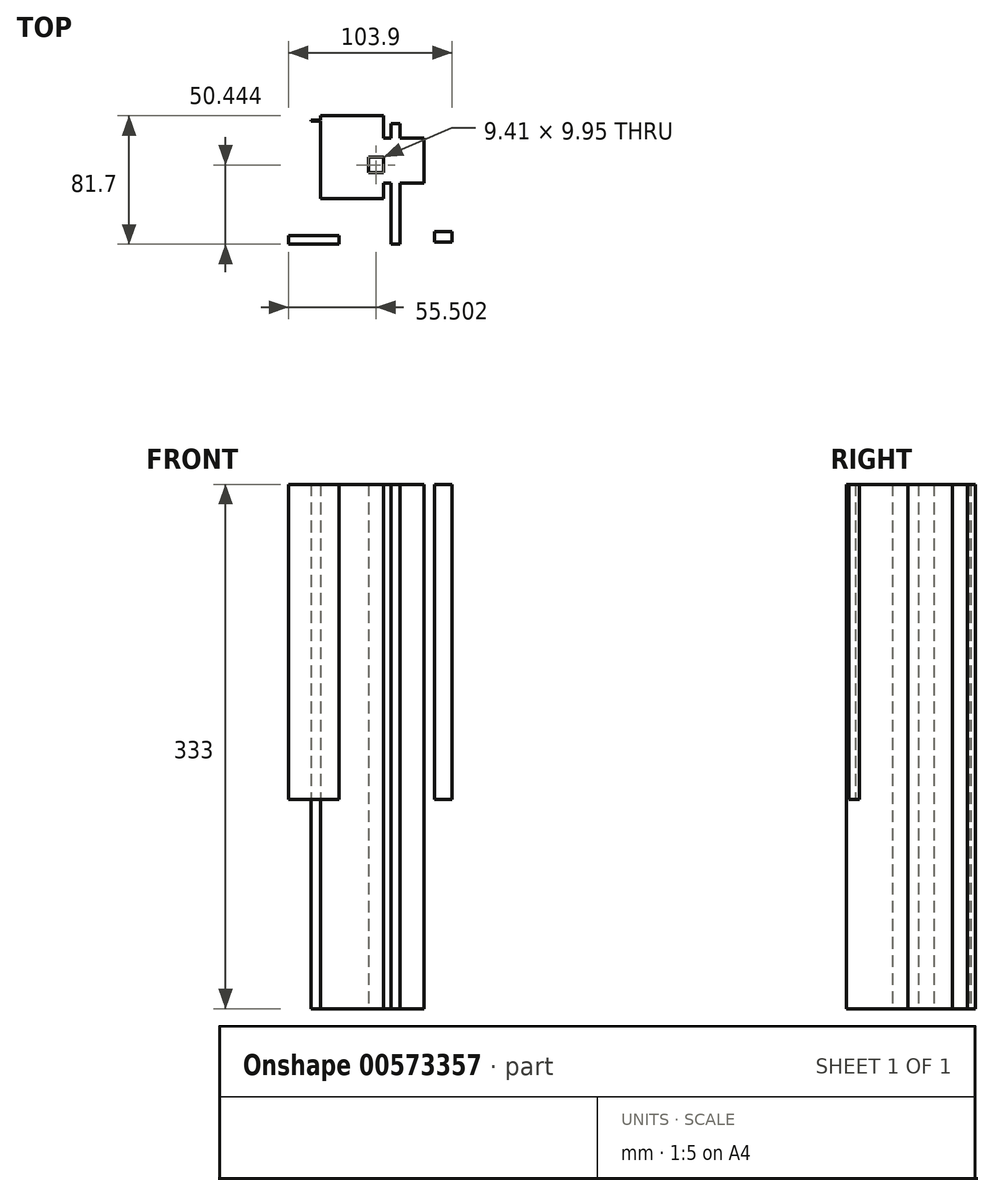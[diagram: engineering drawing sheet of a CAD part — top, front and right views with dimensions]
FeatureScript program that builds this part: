
annotation { "Feature Type Name" : "Feature", "Feature Type Description" : "" }
export const myFeature = defineFeature(function(context is Context, id is Id, definition is map)
    precondition{}
    {
        {
            var Q0;
            Q0=qCreatedBy(makeId("Top.planeOp"),FACE);
            var sketch = newSketch(context, id + "F0", { "sketchPlane" : qUnion([Q0])});
            skLineSegment(sketch, "E0.bottom", {"start": v(33.03, 37.83) * mm, "end": v(38.9, 37.83) * mm});
            skLineSegment(sketch, "E0.top", {"start": v(33.03, -38.9) * mm, "end": v(38.9, -38.9) * mm});
            skLineSegment(sketch, "E0.left", {"start": v(33.03, 37.83) * mm, "end": v(33.03, -38.9) * mm});
            skLineSegment(sketch, "E0.right", {"start": v(38.9, 37.83) * mm, "end": v(38.9, -38.9) * mm});
            skLineSegment(sketch, "E1.bottom", {"start": v(0, -33.21) * mm, "end": v(-31.97, -33.21) * mm});
            skLineSegment(sketch, "E1.top", {"start": v(0, -38.9) * mm, "end": v(-31.97, -38.9) * mm});
            skLineSegment(sketch, "E1.left", {"start": v(0, -33.21) * mm, "end": v(0, -38.9) * mm});
            skLineSegment(sketch, "E1.right", {"start": v(-31.97, -33.21) * mm, "end": v(-31.97, -38.9) * mm});
            skLineSegment(sketch, "E2.bottom", {"start": v(-9.95, 39.25) * mm, "end": v(-17.58, 39.25) * mm});
            skLineSegment(sketch, "E2.top", {"start": v(-9.95, 39.96) * mm, "end": v(-17.58, 39.96) * mm});
            skLineSegment(sketch, "E2.left", {"start": v(-9.95, 39.25) * mm, "end": v(-9.95, 39.96) * mm});
            skLineSegment(sketch, "E2.right", {"start": v(-17.58, 39.25) * mm, "end": v(-17.58, 39.96) * mm});
            skLineSegment(sketch, "E3.bottom", {"start": v(-11.72, -9.77) * mm, "end": v(28.24, -9.77) * mm});
            skLineSegment(sketch, "E3.top", {"start": v(-11.72, 42.8) * mm, "end": v(28.24, 42.8) * mm});
            skLineSegment(sketch, "E3.left", {"start": v(-11.72, -9.77) * mm, "end": v(-11.72, 42.8) * mm});
            skLineSegment(sketch, "E3.right", {"start": v(28.24, -9.77) * mm, "end": v(28.24, 42.8) * mm});
            skPoint(sketch, "E4.oppositeSnap0", {"position": v(28.24, 16.52) * mm});
            skLineSegment(sketch, "E4.bottom", {"start": v(28.24, 6.57) * mm, "end": v(18.83, 6.57) * mm});
            skLineSegment(sketch, "E4.top", {"start": v(28.24, 16.52) * mm, "end": v(18.83, 16.52) * mm});
            skLineSegment(sketch, "E4.left", {"start": v(28.24, 6.57) * mm, "end": v(28.24, 16.52) * mm});
            skLineSegment(sketch, "E4.right", {"start": v(18.83, 6.57) * mm, "end": v(18.83, 16.52) * mm});
            skLineSegment(sketch, "E5.bottom", {"start": v(71.93, -30.73) * mm, "end": v(60.92, -30.73) * mm});
            skLineSegment(sketch, "E5.top", {"start": v(71.93, -37.47) * mm, "end": v(60.92, -37.47) * mm});
            skLineSegment(sketch, "E5.left", {"start": v(71.93, -30.73) * mm, "end": v(71.93, -37.47) * mm});
            skLineSegment(sketch, "E5.right", {"start": v(60.92, -30.73) * mm, "end": v(60.92, -37.47) * mm});
            skLineSegment(sketch, "E6.bottom", {"start": v(54.17, 0) * mm, "end": v(13.68, 0) * mm});
            skLineSegment(sketch, "E6.top", {"start": v(54.17, 28.42) * mm, "end": v(13.68, 28.42) * mm});
            skLineSegment(sketch, "E6.left", {"start": v(54.17, 0) * mm, "end": v(54.17, 28.42) * mm});
            skLineSegment(sketch, "E6.right", {"start": v(13.68, 0) * mm, "end": v(13.68, 28.42) * mm});
            skSolve(sketch);
        }
        {
            var Q0;
            {var subQ1=sQuery(id+"F0.wireOp",EDGE,"E4.bottom");Q0=makeQuery(id+"F0.imprint","IMPRINT",FACE,{"disambiguationData":[TD([[makeQuery(id+"F0.imprint","IMPRINT",EDGE,{"derivedFrom":subQ1}),1.0]])]});}
            var Q1;
            Q1 = qSketchRegion(id + "F0", true);
            extrude(context, id + "F1", {"entities" : qUnion([Q0, Q1]), "depth" : 200 * mm, "offsetDistance" : 25 * mm});
        }
        {
            var Q0;
            Q0=makeQuery(id+"F1.opExtrude","CAP_FACE",FACE,{"disambiguationData":[OSD([sQuery(id+"F0.wireOp",EDGE,"E0.bottom"),sQuery(id+"F0.wireOp",EDGE,"E0.top"),sQuery(id+"F0.wireOp",EDGE,"E0.left"),sQuery(id+"F0.wireOp",EDGE,"E0.right"),sQuery(id+"F0.wireOp",EDGE,"E2.bottom"),sQuery(id+"F0.wireOp",EDGE,"E2.top"),sQuery(id+"F0.wireOp",EDGE,"E2.right"),sQuery(id+"F0.wireOp",EDGE,"E3.bottom"),sQuery(id+"F0.wireOp",EDGE,"E3.top"),sQuery(id+"F0.wireOp",EDGE,"E3.left"),sQuery(id+"F0.wireOp",EDGE,"E3.right"),sQuery(id+"F0.wireOp",EDGE,"E4.bottom"),sQuery(id+"F0.wireOp",EDGE,"E4.top"),sQuery(id+"F0.wireOp",EDGE,"E4.left"),sQuery(id+"F0.wireOp",EDGE,"E4.right"),sQuery(id+"F0.wireOp",EDGE,"E6.bottom"),sQuery(id+"F0.wireOp",EDGE,"E6.top"),sQuery(id+"F0.wireOp",EDGE,"E6.left")])],"isStart":false});
            extrude(context, id + "F2", {"entities" : qUnion([Q0]), "operationType" : NewBodyOperationType.ADD, "oppositeDirection" : true, "depth" : 333 * mm, "offsetDistance" : 25 * mm});
        }
    });
